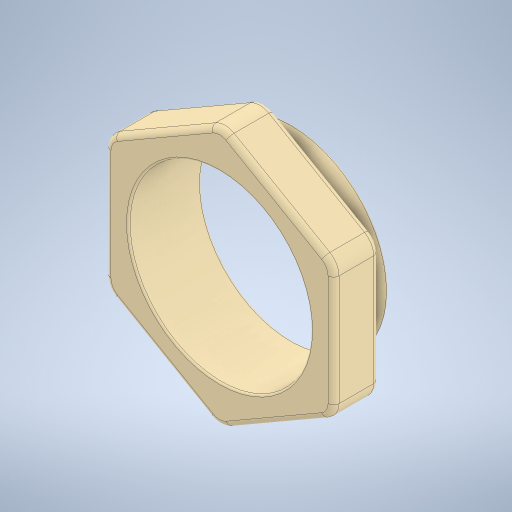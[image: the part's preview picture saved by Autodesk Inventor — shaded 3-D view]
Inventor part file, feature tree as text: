
AUTODESK INVENTOR PART (.ipt)
format: ipt  version: 2024 (Build 280153000, 153)  size: 365,056 bytes
history: native  units: in
note: dims shown in document units (in); Inventor stores cm internally (conversion verified against a paired STEP export)
features: fillet x4, extrude x3, sketch x3, plane x2, direct_edit x1, other x1
ambient origin geometry x8: Origin, YZ Plane, XZ Plane, XY Plane, X Axis, Y Axis, Z Axis, Center Point
bodies: Solid1 (feature_tree)
feature tree (14):
  extrude  "Extrusion1"  Depth=0.075in TaperAngle=0.0deg
  plane  "Work Plane1"
  extrude  "Extrusion2"  Depth=0.625in
  plane  "Work Plane2"
  extrude  "Extrusion3"  TaperAngle=0.0deg  [1 undecoded]
  fillet  "Fillet1"  Radius=0.5in
  fillet  "Fillet2"  Radius=0.21in
  fillet  "Fillet3"  Radius=0.05in
  fillet  "Fillet4"  Radius=0.05in
  direct_edit  "Direct Edit1"
  sketch  "Sketch1"  dims[d0=0.525in d1=0.075in d2=0.0in]
  sketch  "Sketch2"  dims[d3=0.0in d4=0.625in]
  sketch  "Sketch3"  dims[d5=0.125in d6=0.0in d7=0.0in d8=0.5in d9=0.21in d10=0.0in d11=0.05in d12=0.05in d13=0.015in d14=0.005in d15=3.937in d16=0.3937in d17=0.3937in]
  other  "Scale1"
note: 1 required parameter value undecoded (feature->parameter linkage not recoverable at this tier; creation-order binding heuristic only, values carry confidence <= 0.55)
